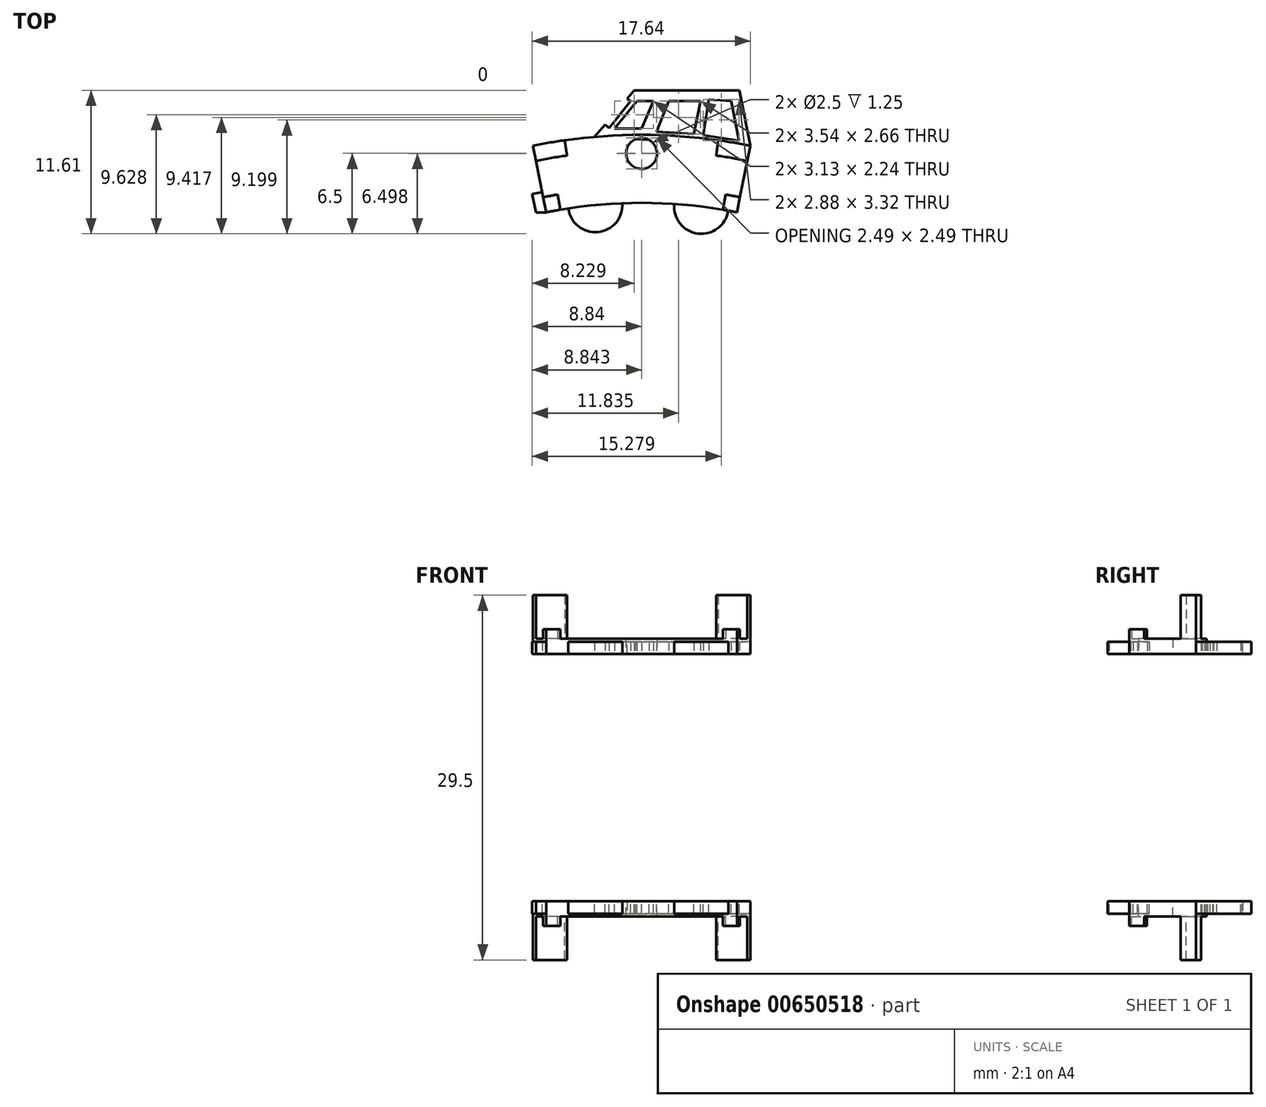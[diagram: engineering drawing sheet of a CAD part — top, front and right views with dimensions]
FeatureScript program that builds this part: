
annotation { "Feature Type Name" : "Feature", "Feature Type Description" : "" }
export const myFeature = defineFeature(function(context is Context, id is Id, definition is map)
    precondition{}
    {
        {
            var Q0;
            Q0=qCreatedBy(makeId("Top.planeOp"),FACE);
            var sketch = newSketch(context, id + "F0", { "sketchPlane" : qUnion([Q0])});
            skCircle(sketch, "E0", {"center": v(0, 0) * mm, "radius": 39 * mm});
            skCircle(sketch, "E1", {"center": v(0, 0) * mm, "radius": 44.5 * mm});
            skCircle(sketch, "E2", {"center": v(0, 43) * mm, "radius": 1.25 * mm});
            skCircle(sketch, "E3", {"center": v(0, 43) * mm, "radius": 6 * mm});
            skLineSegment(sketch, "E4", {"start": v(-7.7, 38.23) * mm, "end": v(-8.8, 43.62) * mm});
            skLineSegment(sketch, "E5", {"start": v(7.7, 38.23) * mm, "end": v(8.8, 43.62) * mm});
            skLineSegment(sketch, "E6", {"start": v(-7.5, 43.86) * mm, "end": v(-6.58, 38.44) * mm});
            skLineSegment(sketch, "E7", {"start": v(6.58, 38.44) * mm, "end": v(7.5, 43.86) * mm});
            skCircle(sketch, "E8", {"center": v(0, 0) * mm, "radius": 40.25 * mm});
            skCircle(sketch, "E9", {"center": v(0, 0) * mm, "radius": 43.25 * mm});
            skSolve(sketch);
        }
        {
            var Q0;
            {var subQ0=sQuery(id+"F0.wireOp",EDGE,"E7");var subQ1=sQuery(id+"F0.wireOp",EDGE,"E1");var subQ2=makeQuery(id+"F0.imprint","INTERSECT",VERTEX,{"derivedFrom":[subQ1,subQ0]});Q0=makeQuery(id+"F0.imprint","IMPRINT",FACE,{"disambiguationData":[TD([[makeQuery(id+"F0.imprint","IMPRINT",EDGE,{"disambiguationData":[TD([[subQ2,-1.0]])],"derivedFrom":subQ1}),1.0]])]});}
            var Q1;
            {var subQ0=sQuery(id+"F0.wireOp",EDGE,"E6");var subQ1=sQuery(id+"F0.wireOp",EDGE,"E1");var subQ2=makeQuery(id+"F0.imprint","INTERSECT",VERTEX,{"derivedFrom":[subQ1,subQ0]});Q1=makeQuery(id+"F0.imprint","IMPRINT",FACE,{"disambiguationData":[TD([[makeQuery(id+"F0.imprint","IMPRINT",EDGE,{"disambiguationData":[TD([[subQ2,1.0]])],"derivedFrom":subQ1}),1.0]])]});}
            var Q2;
            {var subQ0=sQuery(id+"F0.wireOp",EDGE,"E3");var subQ1=sQuery(id+"F0.wireOp",EDGE,"E1");var subQ2=makeQuery(id+"F0.imprint","INTERSECT",VERTEX,{"disambiguationData":[OD(0.0)],"derivedFrom":[subQ1,subQ0]});Q2=makeQuery(id+"F0.imprint","IMPRINT",FACE,{"disambiguationData":[TD([[makeQuery(id+"F0.imprint","IMPRINT",EDGE,{"disambiguationData":[TD([[subQ2,-1.0]])],"derivedFrom":subQ1}),1.0]])]});}
            var Q3;
            {var subQ0=sQuery(id+"F0.wireOp",EDGE,"E8");var subQ1=sQuery(id+"F0.wireOp",EDGE,"E3");var subQ2=makeQuery(id+"F0.imprint","INTERSECT",VERTEX,{"disambiguationData":[OD(1.0)],"derivedFrom":[subQ1,subQ0]});Q3=makeQuery(id+"F0.imprint","IMPRINT",FACE,{"disambiguationData":[TD([[makeQuery(id+"F0.imprint","IMPRINT",EDGE,{"disambiguationData":[TD([[subQ2,-1.0]])],"derivedFrom":subQ1}),-1.0]])]});}
            var Q4;
            {var subQ3=sQuery(id+"F0.wireOp",EDGE,"E9");var subQ5=sQuery(id+"F0.wireOp",EDGE,"E2");var subQ6=makeQuery(id+"F0.imprint","INTERSECT",VERTEX,{"disambiguationData":[OD(0.0)],"derivedFrom":[subQ5,subQ3]});Q4=makeQuery(id+"F0.imprint","IMPRINT",FACE,{"disambiguationData":[TD([[makeQuery(id+"F0.imprint","IMPRINT",EDGE,{"disambiguationData":[TD([[subQ6,1.0]])],"derivedFrom":subQ5}),-1.0]])]});}
            var Q5;
            {var subQ0=sQuery(id+"F0.wireOp",EDGE,"E9");var subQ1=sQuery(id+"F0.wireOp",EDGE,"E3");var subQ2=makeQuery(id+"F0.imprint","INTERSECT",VERTEX,{"disambiguationData":[OD(0.0)],"derivedFrom":[subQ1,subQ0]});Q5=makeQuery(id+"F0.imprint","IMPRINT",FACE,{"disambiguationData":[TD([[makeQuery(id+"F0.imprint","IMPRINT",EDGE,{"disambiguationData":[TD([[subQ2,-1.0]])],"derivedFrom":subQ1}),-1.0]])]});}
            var Q6;
            {var subQ0=sQuery(id+"F0.wireOp",EDGE,"E6");var subQ1=sQuery(id+"F0.wireOp",EDGE,"E0");var subQ2=makeQuery(id+"F0.imprint","INTERSECT",VERTEX,{"derivedFrom":[subQ1,subQ0]});Q6=makeQuery(id+"F0.imprint","IMPRINT",FACE,{"disambiguationData":[TD([[makeQuery(id+"F0.imprint","IMPRINT",EDGE,{"disambiguationData":[TD([[subQ2,1.0]])],"derivedFrom":subQ1}),-1.0]])]});}
            var Q7;
            {var subQ0=sQuery(id+"F0.wireOp",EDGE,"E3");var subQ1=sQuery(id+"F0.wireOp",EDGE,"E0");var subQ2=makeQuery(id+"F0.imprint","INTERSECT",VERTEX,{"disambiguationData":[OD(0.0)],"derivedFrom":[subQ1,subQ0]});Q7=makeQuery(id+"F0.imprint","IMPRINT",FACE,{"disambiguationData":[TD([[makeQuery(id+"F0.imprint","IMPRINT",EDGE,{"disambiguationData":[TD([[subQ2,-1.0]])],"derivedFrom":subQ1}),-1.0]])]});}
            var Q8;
            {var subQ0=sQuery(id+"F0.wireOp",EDGE,"E7");var subQ1=sQuery(id+"F0.wireOp",EDGE,"E0");var subQ2=makeQuery(id+"F0.imprint","INTERSECT",VERTEX,{"derivedFrom":[subQ1,subQ0]});Q8=makeQuery(id+"F0.imprint","IMPRINT",FACE,{"disambiguationData":[TD([[makeQuery(id+"F0.imprint","IMPRINT",EDGE,{"disambiguationData":[TD([[subQ2,-1.0]])],"derivedFrom":subQ1}),-1.0]])]});}
            var Q9;
            {var subQ0=sQuery(id+"F0.wireOp",EDGE,"E8");var subQ1=sQuery(id+"F0.wireOp",EDGE,"E5");var subQ2=makeQuery(id+"F0.imprint","INTERSECT",VERTEX,{"derivedFrom":[subQ1,subQ0]});Q9=makeQuery(id+"F0.imprint","IMPRINT",FACE,{"disambiguationData":[TD([[makeQuery(id+"F0.imprint","IMPRINT",EDGE,{"disambiguationData":[TD([[subQ2,-1.0]])],"derivedFrom":subQ1}),1.0]])]});}
            var Q10;
            {var subQ0=sQuery(id+"F0.wireOp",EDGE,"E8");var subQ1=sQuery(id+"F0.wireOp",EDGE,"E4");var subQ2=makeQuery(id+"F0.imprint","INTERSECT",VERTEX,{"derivedFrom":[subQ1,subQ0]});Q10=makeQuery(id+"F0.imprint","IMPRINT",FACE,{"disambiguationData":[TD([[makeQuery(id+"F0.imprint","IMPRINT",EDGE,{"disambiguationData":[TD([[subQ2,-1.0]])],"derivedFrom":subQ1}),-1.0]])]});}
            extrude(context, id + "F1", {"entities" : qUnion([Q0, Q1, Q2, Q3, Q4, Q5, Q6, Q7, Q8, Q9, Q10]), "depth" : 1.25 * mm, "offsetDistance" : 25 * mm});
        }
        {
            var Q0;
            Q0=qCreatedBy(makeId("Top.planeOp"),FACE);
            var sketch = newSketch(context, id + "F2", { "sketchPlane" : qUnion([Q0])});
            skCircle(sketch, "E10", {"center": v(0, 0) * mm, "radius": 39 * mm});
            skCircle(sketch, "E11", {"center": v(0, 0) * mm, "radius": 44.5 * mm});
            skCircle(sketch, "E12", {"center": v(0, 43) * mm, "radius": 0.85 * mm});
            skCircle(sketch, "E13", {"center": v(0, 43) * mm, "radius": 6 * mm});
            skLineSegment(sketch, "E14", {"start": v(-7.7, 38.23) * mm, "end": v(-8.8, 43.62) * mm});
            skLineSegment(sketch, "E15", {"start": v(7.7, 38.23) * mm, "end": v(8.8, 43.62) * mm});
            skLineSegment(sketch, "E16", {"start": v(-6.2, 44.06) * mm, "end": v(-5.44, 38.62) * mm});
            skLineSegment(sketch, "E17", {"start": v(5.44, 38.62) * mm, "end": v(6.2, 44.06) * mm});
            skCircle(sketch, "E18", {"center": v(0, 0) * mm, "radius": 40.25 * mm});
            skCircle(sketch, "E19", {"center": v(0, 0) * mm, "radius": 43.25 * mm});
            skSolve(sketch);
        }
        {
            var Q0;
            {var subQ0=sQuery(id+"F2.wireOp",EDGE,"E15");var subQ1=sQuery(id+"F2.wireOp",EDGE,"E11");var subQ2=makeQuery(id+"F2.imprint","INTERSECT",VERTEX,{"derivedFrom":[subQ1,subQ0]});Q0=makeQuery(id+"F2.imprint","IMPRINT",FACE,{"disambiguationData":[TD([[makeQuery(id+"F2.imprint","IMPRINT",EDGE,{"disambiguationData":[TD([[subQ2,-1.0]])],"derivedFrom":subQ1}),1.0]])]});}
            var Q1;
            {var subQ0=sQuery(id+"F2.wireOp",EDGE,"E14");var subQ1=sQuery(id+"F2.wireOp",EDGE,"E11");var subQ2=makeQuery(id+"F2.imprint","INTERSECT",VERTEX,{"derivedFrom":[subQ1,subQ0]});Q1=makeQuery(id+"F2.imprint","IMPRINT",FACE,{"disambiguationData":[TD([[makeQuery(id+"F2.imprint","IMPRINT",EDGE,{"disambiguationData":[TD([[subQ2,1.0]])],"derivedFrom":subQ1}),1.0]])]});}
            extrude(context, id + "F3", {"entities" : qUnion([Q0, Q1]), "operationType" : NewBodyOperationType.ADD, "depth" : 4.75 * mm, "offsetDistance" : 25 * mm});
        }
        {
            var Q0;
            Q0=qCreatedBy(makeId("Top.planeOp"),FACE);
            var sketch = newSketch(context, id + "F4", { "sketchPlane" : qUnion([Q0])});
            skCircle(sketch, "E20", {"center": v(0, 0) * mm, "radius": 39 * mm});
            skCircle(sketch, "E21", {"center": v(0, 0) * mm, "radius": 44.5 * mm});
            skCircle(sketch, "E22", {"center": v(0, 43) * mm, "radius": 0.85 * mm});
            skCircle(sketch, "E23", {"center": v(0, 43) * mm, "radius": 6 * mm});
            skLineSegment(sketch, "E24", {"start": v(-7.7, 38.23) * mm, "end": v(-8.8, 43.62) * mm});
            skLineSegment(sketch, "E25", {"start": v(7.7, 38.23) * mm, "end": v(8.8, 43.62) * mm});
            skLineSegment(sketch, "E26", {"start": v(-7.5, 43.86) * mm, "end": v(-6.58, 38.44) * mm});
            skLineSegment(sketch, "E27", {"start": v(6.58, 38.44) * mm, "end": v(7.5, 43.86) * mm});
            skCircle(sketch, "E28", {"center": v(0, 0) * mm, "radius": 40.25 * mm});
            skCircle(sketch, "E29", {"center": v(0, 0) * mm, "radius": 43.25 * mm});
            skSolve(sketch);
        }
        {
            var Q0;
            {var subQ0=sQuery(id+"F4.wireOp",EDGE,"E24");var subQ1=sQuery(id+"F4.wireOp",EDGE,"E20");var subQ2=makeQuery(id+"F4.imprint","INTERSECT",VERTEX,{"derivedFrom":[subQ1,subQ0]});Q0=makeQuery(id+"F4.imprint","IMPRINT",FACE,{"disambiguationData":[TD([[makeQuery(id+"F4.imprint","IMPRINT",EDGE,{"disambiguationData":[TD([[subQ2,1.0]])],"derivedFrom":subQ1}),-1.0]])]});}
            var Q1;
            {var subQ0=sQuery(id+"F4.wireOp",EDGE,"E25");var subQ1=sQuery(id+"F4.wireOp",EDGE,"E20");var subQ2=makeQuery(id+"F4.imprint","INTERSECT",VERTEX,{"derivedFrom":[subQ1,subQ0]});Q1=makeQuery(id+"F4.imprint","IMPRINT",FACE,{"disambiguationData":[TD([[makeQuery(id+"F4.imprint","IMPRINT",EDGE,{"disambiguationData":[TD([[subQ2,-1.0]])],"derivedFrom":subQ1}),-1.0]])]});}
            extrude(context, id + "F5", {"entities" : qUnion([Q0, Q1]), "operationType" : NewBodyOperationType.ADD, "depth" : 2 * mm, "offsetDistance" : 25 * mm});
        }
        {
            var Q0;
            {var subQ0=sQuery(id+"F4.wireOp",EDGE,"E28");var subQ1=sQuery(id+"F4.wireOp",EDGE,"E20");var subQ2=sQuery(id+"F2.wireOp",EDGE,"E19");var subQ3=sQuery(id+"F2.wireOp",EDGE,"E11");Q0=makeQuery(id+"F5.boolean.opBoolean","MERGE",FACE,{"derivedFrom":[makeQuery(id+"F3.boolean.opBoolean","MERGE",FACE,{"derivedFrom":[makeQuery(id+"F1.opExtrude","CAP_FACE",FACE,{"disambiguationData":[OSD([sQuery(id+"F0.wireOp",EDGE,"E0"),sQuery(id+"F0.wireOp",EDGE,"E1"),sQuery(id+"F0.wireOp",EDGE,"E2"),sQuery(id+"F0.wireOp",EDGE,"E4"),sQuery(id+"F0.wireOp",EDGE,"E5"),sQuery(id+"F0.wireOp",EDGE,"E6"),sQuery(id+"F0.wireOp",EDGE,"E7"),sQuery(id+"F0.wireOp",EDGE,"E8"),sQuery(id+"F0.wireOp",EDGE,"E9")])],"isStart":true}),makeQuery(id+"F3.opExtrude","CAP_FACE",FACE,{"disambiguationData":[OSD([subQ3,sQuery(id+"F2.wireOp",EDGE,"E15"),sQuery(id+"F2.wireOp",EDGE,"E17"),subQ2])],"isStart":true}),makeQuery(id+"F3.opExtrude","CAP_FACE",FACE,{"disambiguationData":[OSD([subQ3,sQuery(id+"F2.wireOp",EDGE,"E14"),sQuery(id+"F2.wireOp",EDGE,"E16"),subQ2])],"isStart":true})]}),makeQuery(id+"F5.opExtrude","CAP_FACE",FACE,{"disambiguationData":[OSD([subQ1,sQuery(id+"F4.wireOp",EDGE,"E25"),sQuery(id+"F4.wireOp",EDGE,"E27"),subQ0])],"isStart":true}),makeQuery(id+"F5.opExtrude","CAP_FACE",FACE,{"disambiguationData":[OSD([subQ1,sQuery(id+"F4.wireOp",EDGE,"E24"),sQuery(id+"F4.wireOp",EDGE,"E26"),subQ0])],"isStart":true})]});}
            var sketch = newSketch(context, id + "F6", { "sketchPlane" : qUnion([Q0])});
            skLineSegment(sketch, "E30", {"start": v(8.8, -43.62) * mm, "end": v(7.92, -48.1) * mm});
            skLineSegment(sketch, "E31", {"start": v(7.92, -48.1) * mm, "end": v(-0.59, -48.1) * mm});
            skLineSegment(sketch, "E32", {"start": v(-0.59, -48.1) * mm, "end": v(-3.8, -44.34) * mm});
            skLineSegment(sketch, "E33", {"start": v(-3.8, -44.34) * mm, "end": v(8.8, -43.62) * mm});
            skSolve(sketch);
        }
        {
            var Q0;
            Q0 = qSketchRegion(id + "F6", true);
            extrude(context, id + "F7", {"entities" : qUnion([Q0]), "operationType" : NewBodyOperationType.ADD, "oppositeDirection" : true, "depth" : 1 * mm, "offsetDistance" : 25 * mm});
        }
        {
            var Q0;
            {var subQ0=sQuery(id+"F4.wireOp",EDGE,"E28");var subQ1=sQuery(id+"F4.wireOp",EDGE,"E20");var subQ2=sQuery(id+"F2.wireOp",EDGE,"E19");var subQ3=sQuery(id+"F2.wireOp",EDGE,"E11");Q0=makeQuery(id+"F7.boolean.opBoolean","MERGE",FACE,{"derivedFrom":[makeQuery(id+"F5.boolean.opBoolean","MERGE",FACE,{"derivedFrom":[makeQuery(id+"F3.boolean.opBoolean","MERGE",FACE,{"derivedFrom":[makeQuery(id+"F1.opExtrude","CAP_FACE",FACE,{"disambiguationData":[OSD([sQuery(id+"F0.wireOp",EDGE,"E0"),sQuery(id+"F0.wireOp",EDGE,"E1"),sQuery(id+"F0.wireOp",EDGE,"E2"),sQuery(id+"F0.wireOp",EDGE,"E4"),sQuery(id+"F0.wireOp",EDGE,"E5"),sQuery(id+"F0.wireOp",EDGE,"E6"),sQuery(id+"F0.wireOp",EDGE,"E7"),sQuery(id+"F0.wireOp",EDGE,"E8"),sQuery(id+"F0.wireOp",EDGE,"E9")])],"isStart":true}),makeQuery(id+"F3.opExtrude","CAP_FACE",FACE,{"disambiguationData":[OSD([subQ3,sQuery(id+"F2.wireOp",EDGE,"E15"),sQuery(id+"F2.wireOp",EDGE,"E17"),subQ2])],"isStart":true}),makeQuery(id+"F3.opExtrude","CAP_FACE",FACE,{"disambiguationData":[OSD([subQ3,sQuery(id+"F2.wireOp",EDGE,"E14"),sQuery(id+"F2.wireOp",EDGE,"E16"),subQ2])],"isStart":true})]}),makeQuery(id+"F5.opExtrude","CAP_FACE",FACE,{"disambiguationData":[OSD([subQ1,sQuery(id+"F4.wireOp",EDGE,"E25"),sQuery(id+"F4.wireOp",EDGE,"E27"),subQ0])],"isStart":true}),makeQuery(id+"F5.opExtrude","CAP_FACE",FACE,{"disambiguationData":[OSD([subQ1,sQuery(id+"F4.wireOp",EDGE,"E24"),sQuery(id+"F4.wireOp",EDGE,"E26"),subQ0])],"isStart":true})]}),makeQuery(id+"F7.opExtrude","CAP_FACE",FACE,{"disambiguationData":[OSD([sQuery(id+"F6.wireOp",EDGE,"E30"),sQuery(id+"F6.wireOp",EDGE,"E31"),sQuery(id+"F6.wireOp",EDGE,"E32"),sQuery(id+"F6.wireOp",EDGE,"E33")])],"isStart":true})]});}
            var sketch = newSketch(context, id + "F8", { "sketchPlane" : qUnion([Q0])});
            skLineSegment(sketch, "E34", {"start": v(7.26, -47.25) * mm, "end": v(7.88, -44.04) * mm});
            skLineSegment(sketch, "E35", {"start": v(7.88, -44.04) * mm, "end": v(5, -44.47) * mm});
            skLineSegment(sketch, "E36", {"start": v(5, -44.47) * mm, "end": v(5.43, -47.36) * mm});
            skLineSegment(sketch, "E37", {"start": v(5.43, -47.36) * mm, "end": v(7.26, -47.25) * mm});
            skLineSegment(sketch, "E38", {"start": v(4.76, -47.25) * mm, "end": v(4.24, -44.59) * mm});
            skLineSegment(sketch, "E39", {"start": v(4.24, -44.59) * mm, "end": v(1.23, -44.77) * mm});
            skLineSegment(sketch, "E40", {"start": v(1.23, -44.77) * mm, "end": v(2.2, -47.25) * mm});
            skLineSegment(sketch, "E41", {"start": v(2.2, -47.25) * mm, "end": v(4.76, -47.25) * mm});
            skLineSegment(sketch, "E42", {"start": v(0.95, -47.25) * mm, "end": v(0, -45.01) * mm});
            skLineSegment(sketch, "E43", {"start": v(0, -45.01) * mm, "end": v(-2.18, -45.01) * mm});
            skLineSegment(sketch, "E44", {"start": v(-2.18, -45.01) * mm, "end": v(-0.38, -47.25) * mm});
            skLineSegment(sketch, "E45", {"start": v(-0.38, -47.25) * mm, "end": v(0.95, -47.25) * mm});
            skLineSegment(sketch, "E46", {"start": v(-3.56, -48.91) * mm, "end": v(-0.87, -47.25) * mm});
            skPoint(sketch, "E46.endSnap0", {"position": v(0.29, -47.25) * mm});
            skLineSegment(sketch, "E47", {"start": v(-0.87, -47.25) * mm, "end": v(-2.63, -45.06) * mm});
            skLineSegment(sketch, "E48", {"start": v(-2.63, -45.06) * mm, "end": v(-5.35, -47.25) * mm});
            skLineSegment(sketch, "E49", {"start": v(-5.35, -47.25) * mm, "end": v(-3.56, -48.91) * mm});
            skSolve(sketch);
        }
        {
            var Q0;
            Q0 = qSketchRegion(id + "F8", true);
            extrude(context, id + "F9", {"entities" : qUnion([Q0]), "operationType" : NewBodyOperationType.REMOVE, "oppositeDirection" : true, "depth" : 25 * mm, "offsetDistance" : 25 * mm});
        }
        {
            var Q0;
            {var subQ0=sQuery(id+"F4.wireOp",EDGE,"E28");var subQ1=sQuery(id+"F4.wireOp",EDGE,"E20");var subQ2=sQuery(id+"F2.wireOp",EDGE,"E19");var subQ3=sQuery(id+"F2.wireOp",EDGE,"E11");Q0=makeQuery(id+"F7.boolean.opBoolean","MERGE",FACE,{"derivedFrom":[makeQuery(id+"F5.boolean.opBoolean","MERGE",FACE,{"derivedFrom":[makeQuery(id+"F3.boolean.opBoolean","MERGE",FACE,{"derivedFrom":[makeQuery(id+"F1.opExtrude","CAP_FACE",FACE,{"disambiguationData":[OSD([sQuery(id+"F0.wireOp",EDGE,"E0"),sQuery(id+"F0.wireOp",EDGE,"E1"),sQuery(id+"F0.wireOp",EDGE,"E2"),sQuery(id+"F0.wireOp",EDGE,"E4"),sQuery(id+"F0.wireOp",EDGE,"E5"),sQuery(id+"F0.wireOp",EDGE,"E6"),sQuery(id+"F0.wireOp",EDGE,"E7"),sQuery(id+"F0.wireOp",EDGE,"E8"),sQuery(id+"F0.wireOp",EDGE,"E9")])],"isStart":true}),makeQuery(id+"F3.opExtrude","CAP_FACE",FACE,{"disambiguationData":[OSD([subQ3,sQuery(id+"F2.wireOp",EDGE,"E15"),sQuery(id+"F2.wireOp",EDGE,"E17"),subQ2])],"isStart":true}),makeQuery(id+"F3.opExtrude","CAP_FACE",FACE,{"disambiguationData":[OSD([subQ3,sQuery(id+"F2.wireOp",EDGE,"E14"),sQuery(id+"F2.wireOp",EDGE,"E16"),subQ2])],"isStart":true})]}),makeQuery(id+"F5.opExtrude","CAP_FACE",FACE,{"disambiguationData":[OSD([subQ1,sQuery(id+"F4.wireOp",EDGE,"E25"),sQuery(id+"F4.wireOp",EDGE,"E27"),subQ0])],"isStart":true}),makeQuery(id+"F5.opExtrude","CAP_FACE",FACE,{"disambiguationData":[OSD([subQ1,sQuery(id+"F4.wireOp",EDGE,"E24"),sQuery(id+"F4.wireOp",EDGE,"E26"),subQ0])],"isStart":true})]}),makeQuery(id+"F7.opExtrude","CAP_FACE",FACE,{"disambiguationData":[OSD([sQuery(id+"F6.wireOp",EDGE,"E30"),sQuery(id+"F6.wireOp",EDGE,"E31"),sQuery(id+"F6.wireOp",EDGE,"E32"),sQuery(id+"F6.wireOp",EDGE,"E33")])],"isStart":true})]});}
            var sketch = newSketch(context, id + "F10", { "sketchPlane" : qUnion([Q0])});
            skCircle(sketch, "E50", {"center": v(4.83, -38.7) * mm, "radius": 2.2 * mm});
            skCircle(sketch, "E51", {"center": v(-3.74, -38.82) * mm, "radius": 2.2 * mm});
            skSolve(sketch);
        }
        {
            var Q0;
            Q0 = qSketchRegion(id + "F10", true);
            extrude(context, id + "F11", {"entities" : qUnion([Q0]), "operationType" : NewBodyOperationType.ADD, "oppositeDirection" : true, "depth" : 1 * mm, "offsetDistance" : 25 * mm});
        }
        {
            var Q0;
            {var subQ0=sQuery(id+"F4.wireOp",EDGE,"E28");var subQ1=sQuery(id+"F4.wireOp",EDGE,"E20");var subQ2=sQuery(id+"F2.wireOp",EDGE,"E19");var subQ3=sQuery(id+"F2.wireOp",EDGE,"E11");Q0=makeQuery(id+"F11.boolean.opBoolean","MERGE",FACE,{"derivedFrom":[makeQuery(id+"F7.boolean.opBoolean","MERGE",FACE,{"derivedFrom":[makeQuery(id+"F5.boolean.opBoolean","MERGE",FACE,{"derivedFrom":[makeQuery(id+"F3.boolean.opBoolean","MERGE",FACE,{"derivedFrom":[makeQuery(id+"F1.opExtrude","CAP_FACE",FACE,{"disambiguationData":[OSD([sQuery(id+"F0.wireOp",EDGE,"E0"),sQuery(id+"F0.wireOp",EDGE,"E1"),sQuery(id+"F0.wireOp",EDGE,"E2"),sQuery(id+"F0.wireOp",EDGE,"E4"),sQuery(id+"F0.wireOp",EDGE,"E5"),sQuery(id+"F0.wireOp",EDGE,"E6"),sQuery(id+"F0.wireOp",EDGE,"E7"),sQuery(id+"F0.wireOp",EDGE,"E8"),sQuery(id+"F0.wireOp",EDGE,"E9")])],"isStart":true}),makeQuery(id+"F3.opExtrude","CAP_FACE",FACE,{"disambiguationData":[OSD([subQ3,sQuery(id+"F2.wireOp",EDGE,"E15"),sQuery(id+"F2.wireOp",EDGE,"E17"),subQ2])],"isStart":true}),makeQuery(id+"F3.opExtrude","CAP_FACE",FACE,{"disambiguationData":[OSD([subQ3,sQuery(id+"F2.wireOp",EDGE,"E14"),sQuery(id+"F2.wireOp",EDGE,"E16"),subQ2])],"isStart":true})]}),makeQuery(id+"F5.opExtrude","CAP_FACE",FACE,{"disambiguationData":[OSD([subQ1,sQuery(id+"F4.wireOp",EDGE,"E25"),sQuery(id+"F4.wireOp",EDGE,"E27"),subQ0])],"isStart":true}),makeQuery(id+"F5.opExtrude","CAP_FACE",FACE,{"disambiguationData":[OSD([subQ1,sQuery(id+"F4.wireOp",EDGE,"E24"),sQuery(id+"F4.wireOp",EDGE,"E26"),subQ0])],"isStart":true})]}),makeQuery(id+"F7.opExtrude","CAP_FACE",FACE,{"disambiguationData":[OSD([sQuery(id+"F6.wireOp",EDGE,"E30"),sQuery(id+"F6.wireOp",EDGE,"E31"),sQuery(id+"F6.wireOp",EDGE,"E32"),sQuery(id+"F6.wireOp",EDGE,"E33")])],"isStart":true})]}),makeQuery(id+"F11.opExtrude","CAP_FACE",FACE,{"disambiguationData":[OSD([sQuery(id+"F10.wireOp",EDGE,"E50")])],"isStart":true}),makeQuery(id+"F11.opExtrude","CAP_FACE",FACE,{"disambiguationData":[OSD([sQuery(id+"F10.wireOp",EDGE,"E51")])],"isStart":true})]});}
            var sketch = newSketch(context, id + "F12", { "sketchPlane" : qUnion([Q0])});
            skLineSegment(sketch, "E52", {"start": v(-8.04, -39.86) * mm, "end": v(-8.84, -39.7) * mm});
            skLineSegment(sketch, "E53", {"start": v(-8.84, -39.7) * mm, "end": v(-8.55, -38.23) * mm});
            skLineSegment(sketch, "E54", {"start": v(-8.55, -38.23) * mm, "end": v(-7.7, -38.23) * mm});
            skLineSegment(sketch, "E55", {"start": v(-7.7, -38.23) * mm, "end": v(-8.04, -39.86) * mm});
            skSolve(sketch);
        }
        {
            var Q0;
            Q0=makeQuery(id+"F12.imprint","IMPRINT",FACE,{"disambiguationData":[TD([[makeQuery(id+"F12.imprint","IMPRINT",EDGE,{"derivedFrom":sQuery(id+"F12.wireOp",EDGE,"E52")}),-1.0]])]});
            extrude(context, id + "F13", {"entities" : qUnion([Q0]), "operationType" : NewBodyOperationType.ADD, "oppositeDirection" : true, "depth" : 1 * mm, "offsetDistance" : 25 * mm});
        }
        {
            var Q0;
            Q0=makeQuery(id+"F1.opExtrude","SWEPT_BODY",BODY,{"disambiguationData":[OSD([sQuery(id+"F0.wireOp",EDGE,"E0"),sQuery(id+"F0.wireOp",EDGE,"E1"),sQuery(id+"F0.wireOp",EDGE,"E2"),sQuery(id+"F0.wireOp",EDGE,"E4"),sQuery(id+"F0.wireOp",EDGE,"E5"),sQuery(id+"F0.wireOp",EDGE,"E6"),sQuery(id+"F0.wireOp",EDGE,"E7"),sQuery(id+"F0.wireOp",EDGE,"E8"),sQuery(id+"F0.wireOp",EDGE,"E9")])]});
            transform(context, id + "F14", {"entities" : qUnion([Q0]), "transformType" : TransformType.TRANSLATION_3D, "dx" : 0 * mm, "dy" : 0 * mm, "dz" : 10 * mm, "makeCopy" : false});
        }
        {
            var Q0;
            Q0=makeQuery(id+"F1.opExtrude","SWEPT_BODY",BODY,{"disambiguationData":[OSD([sQuery(id+"F0.wireOp",EDGE,"E0"),sQuery(id+"F0.wireOp",EDGE,"E1"),sQuery(id+"F0.wireOp",EDGE,"E2"),sQuery(id+"F0.wireOp",EDGE,"E4"),sQuery(id+"F0.wireOp",EDGE,"E5"),sQuery(id+"F0.wireOp",EDGE,"E6"),sQuery(id+"F0.wireOp",EDGE,"E7"),sQuery(id+"F0.wireOp",EDGE,"E8"),sQuery(id+"F0.wireOp",EDGE,"E9")])]});
            var Q1;
            Q1=qCreatedBy(makeId("Top.planeOp"),FACE);
            mirror(context, id + "F15", {"entities" : qUnion([Q0]), "mirrorPlane" : qUnion([Q1])});
        }
    });
